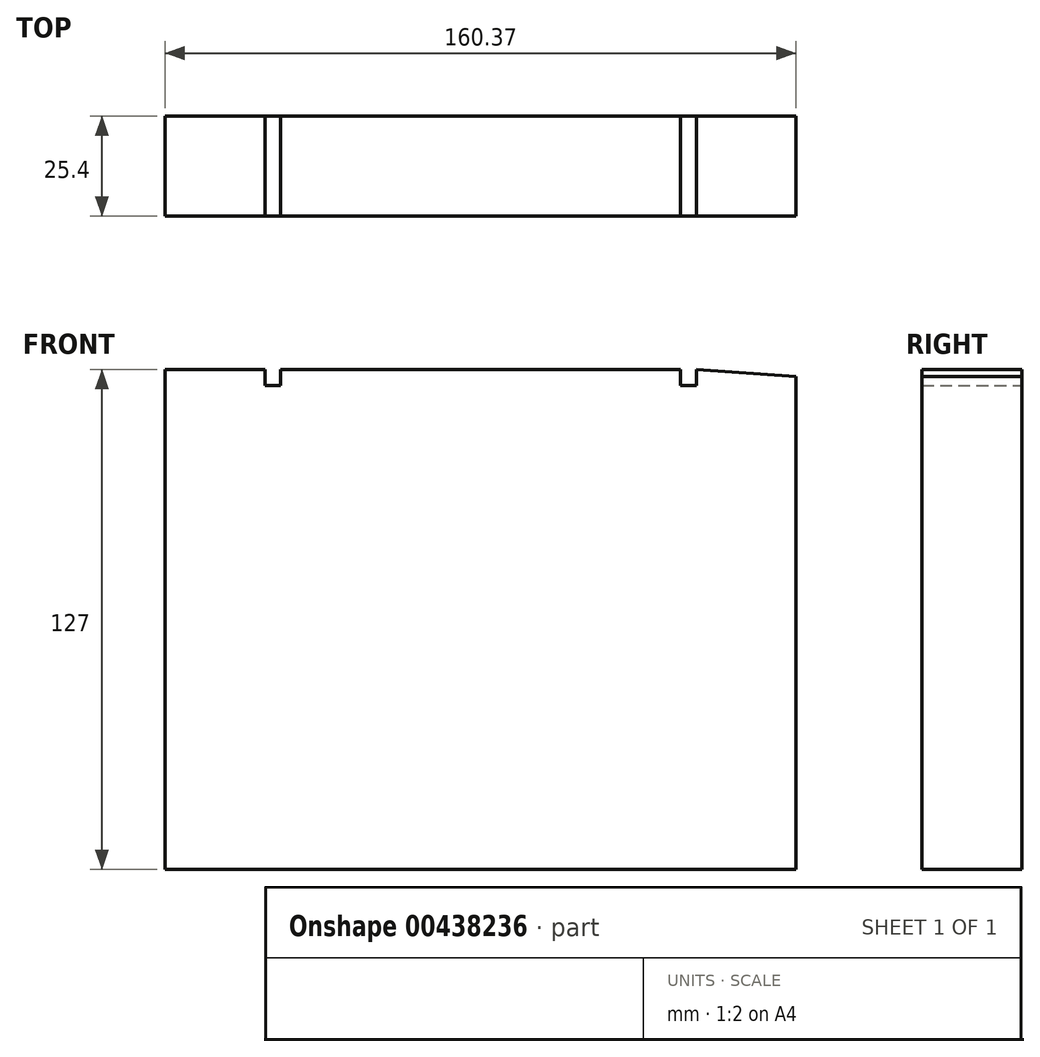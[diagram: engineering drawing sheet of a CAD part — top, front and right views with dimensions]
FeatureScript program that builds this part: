
annotation { "Feature Type Name" : "Feature", "Feature Type Description" : "" }
export const myFeature = defineFeature(function(context is Context, id is Id, definition is map)
    precondition{}
    {
        {
            var Q0;
            Q0=qCreatedBy(makeId("Front.planeOp"),FACE);
            var sketch = newSketch(context, id + "F0", { "sketchPlane" : qUnion([Q0])});
            skLineSegment(sketch, "E0", {"start": v(-489.74, 53.67) * mm, "end": v(-489.71, -71.46) * mm});
            skLineSegment(sketch, "E1", {"start": v(-489.71, -71.46) * mm, "end": v(-650.08, -71.5) * mm});
            skLineSegment(sketch, "E2", {"start": v(-650.08, -71.5) * mm, "end": v(-650.08, 55.5) * mm});
            skLineSegment(sketch, "E3", {"start": v(-650.08, 55.5) * mm, "end": v(-624.68, 55.5) * mm});
            skLineSegment(sketch, "E4", {"start": v(-624.68, 55.5) * mm, "end": v(-624.68, 51.5) * mm});
            skLineSegment(sketch, "E5", {"start": v(-624.68, 51.5) * mm, "end": v(-620.68, 51.5) * mm});
            skLineSegment(sketch, "E6", {"start": v(-620.68, 51.5) * mm, "end": v(-620.68, 55.5) * mm});
            skLineSegment(sketch, "E7", {"start": v(-620.68, 55.5) * mm, "end": v(-519.08, 55.5) * mm});
            skLineSegment(sketch, "E8", {"start": v(-519.08, 55.5) * mm, "end": v(-519.08, 51.5) * mm});
            skLineSegment(sketch, "E9", {"start": v(-519.08, 51.5) * mm, "end": v(-515.08, 51.5) * mm});
            skLineSegment(sketch, "E10", {"start": v(-515.08, 51.5) * mm, "end": v(-515.08, 55.5) * mm});
            skLineSegment(sketch, "E11", {"start": v(-515.08, 55.5) * mm, "end": v(-489.74, 53.67) * mm});
            skSolve(sketch);
        }
        {
            var Q0;
            Q0=makeQuery(id+"F0.imprint","IMPRINT",FACE,{"disambiguationData":[TD([[makeQuery(id+"F0.imprint","IMPRINT",EDGE,{"derivedFrom":sQuery(id+"F0.wireOp",EDGE,"E0")}),-1.0]])]});
            extrude(context, id + "F1", {"entities" : qUnion([Q0]), "depth" : 25.4 * mm});
        }
    });
